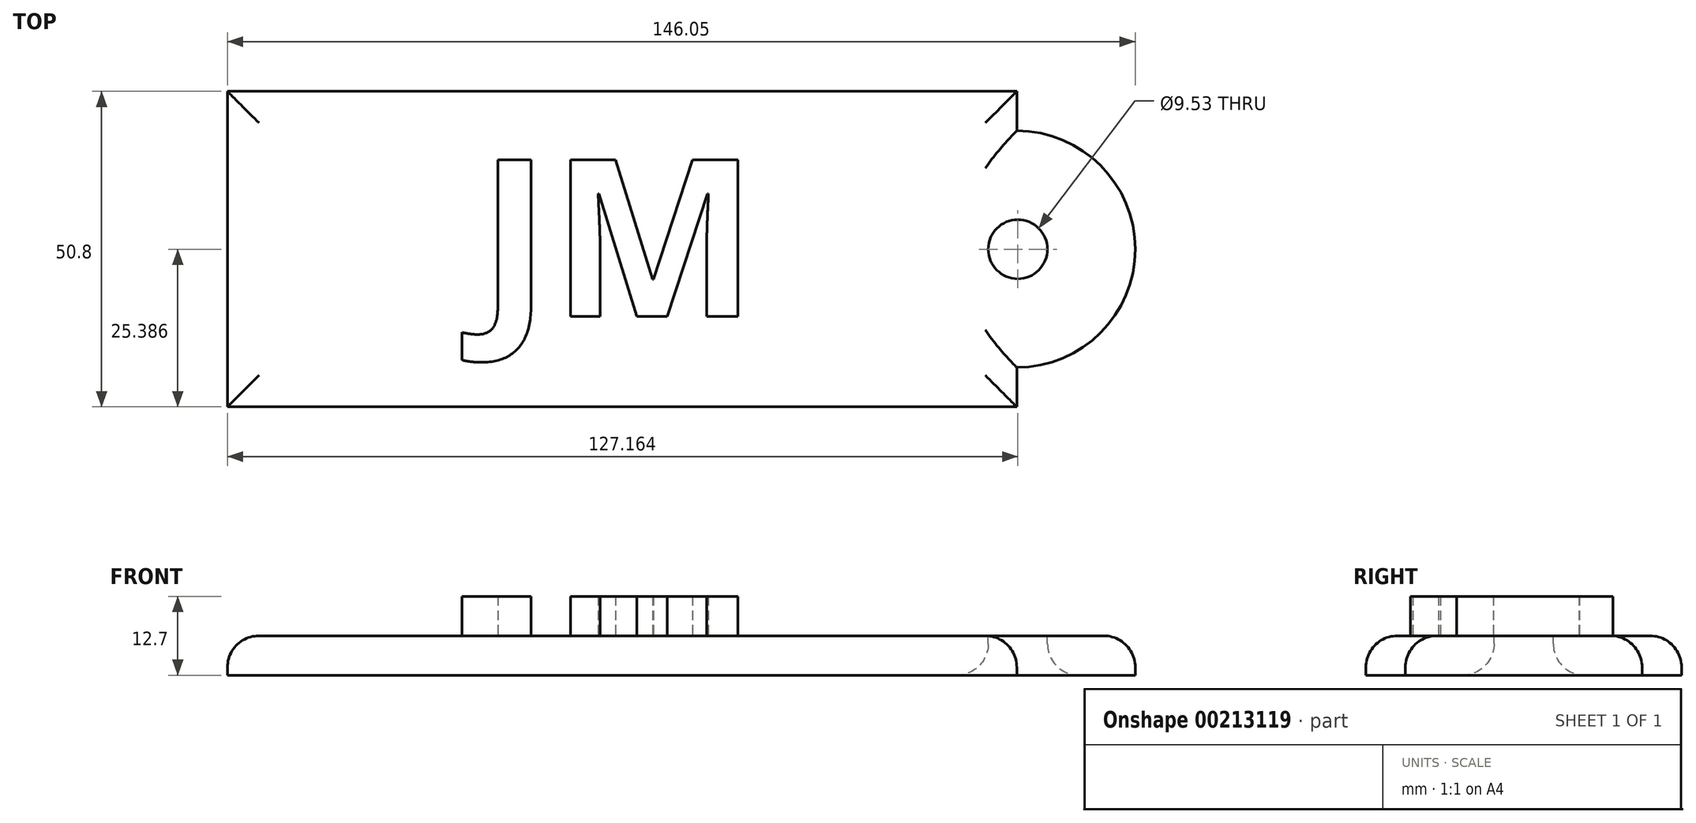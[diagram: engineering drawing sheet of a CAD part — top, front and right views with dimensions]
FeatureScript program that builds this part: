
annotation { "Feature Type Name" : "Feature", "Feature Type Description" : "" }
export const myFeature = defineFeature(function(context is Context, id is Id, definition is map)
    precondition{}
    {
        {
            var Q0;
            Q0=qCreatedBy(makeId("Top.planeOp"),FACE);
            var sketch = newSketch(context, id + "F0", { "sketchPlane" : qUnion([Q0])});
            skLineSegment(sketch, "E0.bottom", {"start": v(0, 0) * mm, "end": v(127, 0) * mm});
            skLineSegment(sketch, "E0.top", {"start": v(0, 50.8) * mm, "end": v(127, 50.8) * mm});
            skLineSegment(sketch, "E0.left", {"start": v(0, 0) * mm, "end": v(0, 50.8) * mm});
            skLineSegment(sketch, "E0.right", {"start": v(127, 0) * mm, "end": v(127, 50.8) * mm});
            skSolve(sketch);
        }
        {
            var Q0;
            Q0=makeQuery(id+"F0.imprint","IMPRINT",FACE,{"disambiguationData":[TD([[makeQuery(id+"F0.imprint","IMPRINT",EDGE,{"derivedFrom":sQuery(id+"F0.wireOp",EDGE,"E0.bottom")}),1.0]])]});
            extrude(context, id + "F1", {"entities" : qUnion([Q0]), "depth" : 6.35 * mm});
        }
        {
            var Q0;
            Q0=makeQuery(id+"F1.opExtrude","CAP_FACE",FACE,{"disambiguationData":[OSD([sQuery(id+"F0.wireOp",EDGE,"E0.bottom"),sQuery(id+"F0.wireOp",EDGE,"E0.top"),sQuery(id+"F0.wireOp",EDGE,"E0.left"),sQuery(id+"F0.wireOp",EDGE,"E0.right")])],"isStart":false});
            var sketch = newSketch(context, id + "F2", { "sketchPlane" : qUnion([Q0])});
            skCircle(sketch, "E1", {"center": v(127, 25.4) * mm, "radius": 19.05 * mm});
            skSolve(sketch);
        }
        {
            var Q0;
            {var subQ0=sQuery(id+"F2.wireOp",EDGE,"E1");var subQ1=makeQuery(id+"F1.opExtrude","CAP_EDGE",EDGE,{"disambiguationData":[OSD([sQuery(id+"F0.wireOp",EDGE,"E0.right")])],"isStart":false});var subQ2=makeQuery(id+"F2.imprint","INTERSECT",VERTEX,{"disambiguationData":[OD(0.0)],"derivedFrom":[subQ1,subQ0]});Q0=makeQuery(id+"F2.imprint","IMPRINT",FACE,{"disambiguationData":[TD([[makeQuery(id+"F2.imprint","IMPRINT",EDGE,{"disambiguationData":[TD([[subQ2,-1.0]])],"derivedFrom":subQ0}),1.0]])]});}
            extrude(context, id + "F3", {"entities" : qUnion([Q0]), "operationType" : NewBodyOperationType.ADD, "oppositeDirection" : true, "depth" : 6.35 * mm});
        }
        {
            var Q0;
            {var subQ0=sQuery(id+"F0.wireOp",EDGE,"E0.right");Q0=makeQuery(id+"F3.boolean.opBoolean","MERGE",FACE,{"derivedFrom":[makeQuery(id+"F1.opExtrude","CAP_FACE",FACE,{"disambiguationData":[OSD([sQuery(id+"F0.wireOp",EDGE,"E0.bottom"),sQuery(id+"F0.wireOp",EDGE,"E0.top"),sQuery(id+"F0.wireOp",EDGE,"E0.left"),subQ0])],"isStart":false}),makeQuery(id+"F3.opExtrude","CAP_FACE",FACE,{"disambiguationData":[OSD([subQ0,sQuery(id+"F2.wireOp",EDGE,"E1")])],"isStart":true})]});}
            var sketch = newSketch(context, id + "F4", { "sketchPlane" : qUnion([Q0])});
            skText(sketch, "E2", { "text": "JM", "fontName": "OpenSans-Bold.ttf"});
            const initialGuessF4  = {"E2": [0.04033, 0.01459, 1, 0, 0.0254]};
            skSetInitialGuess(sketch, initialGuessF4);
            skSolve(sketch);
        }
        {
            var Q0;
            Q0=makeQuery(id+"F4.imprint","IMPRINT",FACE,{"disambiguationData":[TD([[makeQuery(id+"F4.imprint","IMPRINT",EDGE,{"derivedFrom":sQuery(id+"F4.wireOp",EDGE,"E2.sketch_text.stroke-0")}),1.0]])]});
            var sketch = newSketch(context, id + "F5", { "sketchPlane" : qUnion([Q0])});
            skCircle(sketch, "E3", {"center": v(127.16, 25.39) * mm, "radius": 4.76 * mm});
            skSolve(sketch);
        }
        {
            var Q0;
            Q0 = qSketchRegion(id + "F5", true);
            extrude(context, id + "F6", {"entities" : qUnion([Q0]), "operationType" : NewBodyOperationType.REMOVE, "endBound" : BoundingType.THROUGH_ALL, "oppositeDirection" : true, "depth" : 25.4 * mm});
        }
        {
            var Q0;
            Q0 = qSketchRegion(id + "F4", true);
            extrude(context, id + "F7", {"entities" : qUnion([Q0]), "operationType" : NewBodyOperationType.ADD, "depth" : 6.35 * mm});
        }
        {
            var Q0;
            {var subQ1=sQuery(id+"F0.wireOp",EDGE,"E0.right");var subQ2=sQuery(id+"F0.wireOp",EDGE,"E0.top");Q0=makeQuery(id+"F3.boolean.opBoolean","SPLIT",EDGE,{"disambiguationData":[TD([makeQuery(id+"F1.opExtrude","SWEPT_FACE",FACE,{"disambiguationData":[OSD([subQ2])]})])],"derivedFrom":makeQuery(id+"F1.opExtrude","CAP_EDGE",EDGE,{"disambiguationData":[OSD([subQ1])],"isStart":false})});}
            var Q1;
            Q1=makeQuery(id+"F3.opExtrude","CAP_EDGE",EDGE,{"disambiguationData":[OSD([sQuery(id+"F2.wireOp",EDGE,"E1")])],"isStart":true});
            var Q2;
            {var subQ0=sQuery(id+"F0.wireOp",EDGE,"E0.right");var subQ2=sQuery(id+"F0.wireOp",EDGE,"E0.bottom");Q2=makeQuery(id+"F3.boolean.opBoolean","SPLIT",EDGE,{"disambiguationData":[TD([makeQuery(id+"F1.opExtrude","SWEPT_FACE",FACE,{"disambiguationData":[OSD([subQ2])]})])],"derivedFrom":makeQuery(id+"F1.opExtrude","CAP_EDGE",EDGE,{"disambiguationData":[OSD([subQ0])],"isStart":false})});}
            var Q3;
            Q3=makeQuery(id+"F1.opExtrude","CAP_EDGE",EDGE,{"disambiguationData":[OSD([sQuery(id+"F0.wireOp",EDGE,"E0.bottom")])],"isStart":false});
            var Q4;
            Q4=makeQuery(id+"F1.opExtrude","CAP_EDGE",EDGE,{"disambiguationData":[OSD([sQuery(id+"F0.wireOp",EDGE,"E0.top")])],"isStart":false});
            var Q5;
            Q5=makeQuery(id+"F1.opExtrude","CAP_EDGE",EDGE,{"disambiguationData":[OSD([sQuery(id+"F0.wireOp",EDGE,"E0.left")])],"isStart":false});
            var Q6;
            {var subQ0=sQuery(id+"F0.wireOp",EDGE,"E0.right");Q6=makeQuery(id+"F6.boolean.opBoolean","INTERSECT",EDGE,{"derivedFrom":[makeQuery(id+"F3.boolean.opBoolean","MERGE",FACE,{"derivedFrom":[makeQuery(id+"F1.opExtrude","CAP_FACE",FACE,{"disambiguationData":[OSD([sQuery(id+"F0.wireOp",EDGE,"E0.bottom"),sQuery(id+"F0.wireOp",EDGE,"E0.top"),sQuery(id+"F0.wireOp",EDGE,"E0.left"),subQ0])],"isStart":true}),makeQuery(id+"F3.opExtrude","CAP_FACE",FACE,{"disambiguationData":[OSD([subQ0,sQuery(id+"F2.wireOp",EDGE,"E1")])],"isStart":false})]}),makeQuery(id+"F6.opExtrude","SWEPT_FACE",FACE,{"disambiguationData":[OSD([sQuery(id+"F5.wireOp",EDGE,"E3")])]})]});}
            fillet(context, id + "F8", {"entities" : qUnion([Q0, Q1, Q2, Q3, Q4, Q5, Q6]), "radius" : 5.08 * mm, "tangentPropagation" : true, "allowEdgeOverflow" : false});
        }
    });
